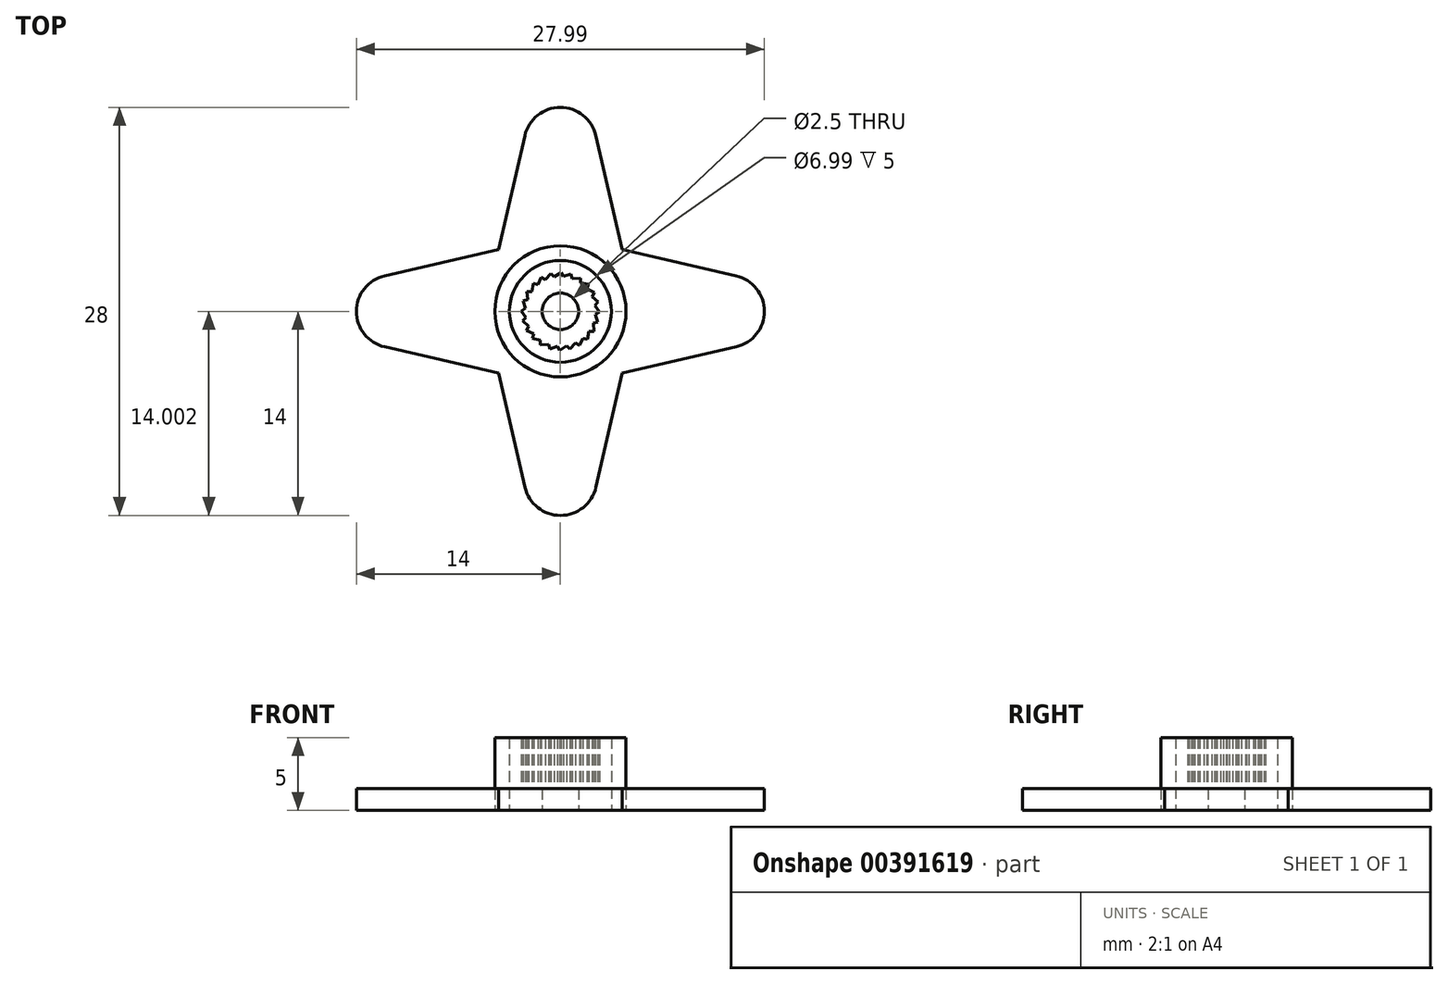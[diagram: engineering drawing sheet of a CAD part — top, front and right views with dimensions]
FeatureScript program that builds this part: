
annotation { "Feature Type Name" : "Feature", "Feature Type Description" : "" }
export const myFeature = defineFeature(function(context is Context, id is Id, definition is map)
    precondition{}
    {
        {
            var Q0;
            Q0=qCreatedBy(makeId("Top.planeOp"),FACE);
            var sketch = newSketch(context, id + "F0", { "sketchPlane" : qUnion([Q0])});
            skLineSegment(sketch, "E0", {"start": v(4.25, -4.24) * mm, "end": v(2.44, -12.07) * mm});
            skLineSegment(sketch, "E1", {"start": v(4.25, -4.24) * mm, "end": v(12.07, -2.44) * mm});
            skLineSegment(sketch, "E2", {"start": v(12.06, 2.43) * mm, "end": v(4.24, 4.24) * mm});
            skLineSegment(sketch, "E3", {"start": v(4.24, 4.24) * mm, "end": v(2.43, 12.06) * mm});
            skArc(sketch, "E4", {"start": v(12.07, -2.44) * mm, "mid": v(14, 0) * mm, "end": v(12.06, 2.43) * mm});
            skLineSegment(sketch, "E5.MirrorCS", {"start": v(-4.24, -4.24) * mm, "end": v(-2.43, -12.07) * mm});
            skLineSegment(sketch, "E6.MirrorCS", {"start": v(-4.24, -4.24) * mm, "end": v(-12.06, -2.44) * mm});
            skLineSegment(sketch, "E7.MirrorCS", {"start": v(-12.06, 2.44) * mm, "end": v(-4.24, 4.24) * mm});
            skArc(sketch, "E8.MirrorCS", {"start": v(-12.06, -2.44) * mm, "mid": v(-14, 0) * mm, "end": v(-12.06, 2.44) * mm});
            skArc(sketch, "E9", {"start": v(2.43, 12.06) * mm, "mid": v(0, 14) * mm, "end": v(-2.44, 12.06) * mm});
            skArc(sketch, "E10", {"start": v(-2.43, -12.07) * mm, "mid": v(0, -14) * mm, "end": v(2.44, -12.07) * mm});
            skLineSegment(sketch, "E11", {"start": v(-2.44, 12.06) * mm, "end": v(-4.24, 4.24) * mm});
            skCircle(sketch, "E12", {"center": v(0, 0) * mm, "radius": 1.25 * mm});
            skCircle(sketch, "E13", {"center": v(0, 0) * mm, "radius": 2.5 * mm});
            skCircle(sketch, "E14.0", {"center": v(0, 0) * mm, "radius": 4.5 * mm});
            skSolve(sketch);
        }
        {
            var Q0;
            Q0=qCreatedBy(makeId("Top.planeOp"),FACE);
            var sketch = newSketch(context, id + "F1", { "sketchPlane" : qUnion([Q0])});
            skPoint(sketch, "E15.0", {"position": v(-0.74, -0.66) * mm});
            skPoint(sketch, "E16.0", {"position": v(0.66, 0.75) * mm});
            skPoint(sketch, "E17.0", {"position": v(0.66, -0.75) * mm});
            skPoint(sketch, "E18.0", {"position": v(-0.56, 0.83) * mm});
            skCircle(sketch, "E19", {"center": v(0, 0) * mm, "radius": 1 * mm});
            skCircle(sketch, "E20", {"center": v(0, 0) * mm, "radius": 3.5 * mm});
            skLineSegment(sketch, "E21.24", {"start": v(2.78, 0.66) * mm, "end": v(2.53, 0.4) * mm});
            skCircle(sketch, "E22.0", {"center": v(0, 0) * mm, "radius": 4.5 * mm});
            skLineSegment(sketch, "E23.0", {"start": v(2.36, 0.42) * mm, "end": v(2.67, -0.04) * mm});
            skLineSegment(sketch, "E23.1", {"start": v(2.59, 0.65) * mm, "end": v(2.36, 0.42) * mm});
            skLineSegment(sketch, "E23.2", {"start": v(-2.17, -1.02) * mm, "end": v(-2.59, -0.66) * mm});
            skLineSegment(sketch, "E23.3", {"start": v(-2.33, -1.3) * mm, "end": v(-2.17, -1.02) * mm});
            skLineSegment(sketch, "E23.4", {"start": v(-1.84, -1.55) * mm, "end": v(-2.33, -1.3) * mm});
            skLineSegment(sketch, "E23.5", {"start": v(-1.92, -1.86) * mm, "end": v(-1.84, -1.55) * mm});
            skLineSegment(sketch, "E23.6", {"start": v(-1.37, -1.97) * mm, "end": v(-1.92, -1.86) * mm});
            skLineSegment(sketch, "E23.7", {"start": v(-1.37, -2.3) * mm, "end": v(-1.37, -1.97) * mm});
            skLineSegment(sketch, "E23.8", {"start": v(-0.82, -2.26) * mm, "end": v(-1.37, -2.3) * mm});
            skLineSegment(sketch, "E23.9", {"start": v(-0.73, -2.57) * mm, "end": v(-0.82, -2.26) * mm});
            skLineSegment(sketch, "E23.10", {"start": v(-0.2, -2.4) * mm, "end": v(-0.73, -2.57) * mm});
            skLineSegment(sketch, "E23.11", {"start": v(-0.04, -2.67) * mm, "end": v(-0.2, -2.4) * mm});
            skLineSegment(sketch, "E23.12", {"start": v(0.42, -2.37) * mm, "end": v(-0.04, -2.67) * mm});
            skLineSegment(sketch, "E23.13", {"start": v(0.65, -2.6) * mm, "end": v(0.42, -2.37) * mm});
            skLineSegment(sketch, "E23.14", {"start": v(2.26, -0.82) * mm, "end": v(2.3, -1.37) * mm});
            skLineSegment(sketch, "E23.15", {"start": v(2.57, -0.73) * mm, "end": v(2.26, -0.82) * mm});
            skLineSegment(sketch, "E23.16", {"start": v(2.39, -0.2) * mm, "end": v(2.57, -0.73) * mm});
            skLineSegment(sketch, "E23.17", {"start": v(2.67, -0.04) * mm, "end": v(2.39, -0.2) * mm});
            skLineSegment(sketch, "E23.18", {"start": v(2.3, -1.37) * mm, "end": v(1.97, -1.38) * mm});
            skLineSegment(sketch, "E23.19", {"start": v(1.97, -1.38) * mm, "end": v(1.86, -1.92) * mm});
            skLineSegment(sketch, "E23.20", {"start": v(1.86, -1.92) * mm, "end": v(1.54, -1.84) * mm});
            skLineSegment(sketch, "E23.21", {"start": v(1.54, -1.84) * mm, "end": v(1.3, -2.34) * mm});
            skLineSegment(sketch, "E23.22", {"start": v(1.3, -2.34) * mm, "end": v(1.02, -2.18) * mm});
            skLineSegment(sketch, "E23.23", {"start": v(1.02, -2.18) * mm, "end": v(0.65, -2.6) * mm});
            skLineSegment(sketch, "E23.24", {"start": v(-2.59, -0.66) * mm, "end": v(-2.36, -0.42) * mm});
            skLineSegment(sketch, "E23.25", {"start": v(-2.36, -0.42) * mm, "end": v(-2.67, 0.03) * mm});
            skLineSegment(sketch, "E23.26", {"start": v(-2.67, 0.03) * mm, "end": v(-2.4, 0.2) * mm});
            skLineSegment(sketch, "E23.27", {"start": v(-2.4, 0.2) * mm, "end": v(-2.57, 0.72) * mm});
            skLineSegment(sketch, "E23.28", {"start": v(-2.57, 0.72) * mm, "end": v(-2.26, 0.81) * mm});
            skLineSegment(sketch, "E23.29", {"start": v(-2.26, 0.81) * mm, "end": v(-2.3, 1.36) * mm});
            skLineSegment(sketch, "E23.30", {"start": v(-2.3, 1.36) * mm, "end": v(-1.97, 1.37) * mm});
            skLineSegment(sketch, "E23.31", {"start": v(-1.97, 1.37) * mm, "end": v(-1.86, 1.91) * mm});
            skLineSegment(sketch, "E23.32", {"start": v(-1.86, 1.91) * mm, "end": v(-1.54, 1.83) * mm});
            skLineSegment(sketch, "E23.33", {"start": v(-1.54, 1.83) * mm, "end": v(-1.3, 2.33) * mm});
            skLineSegment(sketch, "E23.34", {"start": v(-1.3, 2.33) * mm, "end": v(-1.02, 2.17) * mm});
            skLineSegment(sketch, "E23.35", {"start": v(-1.02, 2.17) * mm, "end": v(-0.65, 2.59) * mm});
            skLineSegment(sketch, "E23.36", {"start": v(-0.65, 2.59) * mm, "end": v(-0.42, 2.36) * mm});
            skLineSegment(sketch, "E23.37", {"start": v(-0.42, 2.36) * mm, "end": v(0.04, 2.67) * mm});
            skLineSegment(sketch, "E23.38", {"start": v(0.04, 2.67) * mm, "end": v(0.2, 2.39) * mm});
            skLineSegment(sketch, "E23.39", {"start": v(0.2, 2.39) * mm, "end": v(0.73, 2.57) * mm});
            skLineSegment(sketch, "E23.40", {"start": v(0.73, 2.57) * mm, "end": v(0.82, 2.25) * mm});
            skLineSegment(sketch, "E23.41", {"start": v(0.82, 2.25) * mm, "end": v(1.37, 2.29) * mm});
            skLineSegment(sketch, "E23.42", {"start": v(1.37, 2.29) * mm, "end": v(1.37, 1.96) * mm});
            skLineSegment(sketch, "E23.43", {"start": v(1.37, 1.96) * mm, "end": v(1.91, 1.86) * mm});
            skLineSegment(sketch, "E23.44", {"start": v(1.91, 1.86) * mm, "end": v(1.84, 1.54) * mm});
            skLineSegment(sketch, "E23.45", {"start": v(1.84, 1.54) * mm, "end": v(2.33, 1.3) * mm});
            skLineSegment(sketch, "E23.46", {"start": v(2.33, 1.3) * mm, "end": v(2.17, 1.01) * mm});
            skLineSegment(sketch, "E23.47", {"start": v(2.17, 1.01) * mm, "end": v(2.59, 0.65) * mm});
            skCircle(sketch, "E24.0", {"center": v(0, 0) * mm, "radius": 3.04 * mm});
            skSolve(sketch);
        }
        {
            var Q0;
            Q0=makeQuery(id+"F1.imprint","IMPRINT",FACE,{"disambiguationData":[TD([[makeQuery(id+"F1.imprint","IMPRINT",EDGE,{"derivedFrom":sQuery(id+"F1.wireOp",EDGE,"E20")}),1.0]])]});
            extrude(context, id + "F2", {"entities" : qUnion([Q0]), "depth" : 5 * mm});
        }
        {
            var Q0;
            Q0=makeQuery(id+"F1.imprint","IMPRINT",FACE,{"disambiguationData":[TD([[makeQuery(id+"F1.imprint","IMPRINT",EDGE,{"derivedFrom":sQuery(id+"F1.wireOp",EDGE,"E20")}),-1.0]])]});
            extrude(context, id + "F3", {"entities" : qUnion([Q0]), "depth" : 5 * mm});
        }
        {
            var Q0;
            Q0=makeQuery(id+"F0.imprint","IMPRINT",FACE,{"disambiguationData":[TD([[makeQuery(id+"F0.imprint","IMPRINT",EDGE,{"derivedFrom":sQuery(id+"F0.wireOp",EDGE,"E0")}),-1.0]])]});
            var Q1;
            Q1=makeQuery(id+"F1.imprint","IMPRINT",FACE,{"disambiguationData":[TD([[makeQuery(id+"F1.imprint","IMPRINT",EDGE,{"derivedFrom":sQuery(id+"F1.wireOp",EDGE,"E20")}),1.0]])]});
            var Q2;
            Q2=makeQuery(id+"F0.imprint","IMPRINT",FACE,{"disambiguationData":[TD([[makeQuery(id+"F0.imprint","IMPRINT",EDGE,{"derivedFrom":sQuery(id+"F0.wireOp",EDGE,"E13")}),-1.0]])]});
            var Q3;
            Q3=makeQuery(id+"F0.imprint","IMPRINT",FACE,{"disambiguationData":[TD([[makeQuery(id+"F0.imprint","IMPRINT",EDGE,{"derivedFrom":sQuery(id+"F0.wireOp",EDGE,"E12")}),-1.0]])]});
            extrude(context, id + "F4", {"entities" : qUnion([Q0, Q1, Q2, Q3]), "depth" : 1.5 * mm});
        }
        {
            var Q0;
            Q0=makeQuery(id+"F1.imprint","IMPRINT",FACE,{"disambiguationData":[TD([[makeQuery(id+"F1.imprint","IMPRINT",EDGE,{"derivedFrom":sQuery(id+"F1.wireOp",EDGE,"E23.0")}),1.0]])]});
            extrude(context, id + "F5", {"entities" : qUnion([Q0]), "operationType" : NewBodyOperationType.ADD, "depth" : 5 * mm});
        }
    });
